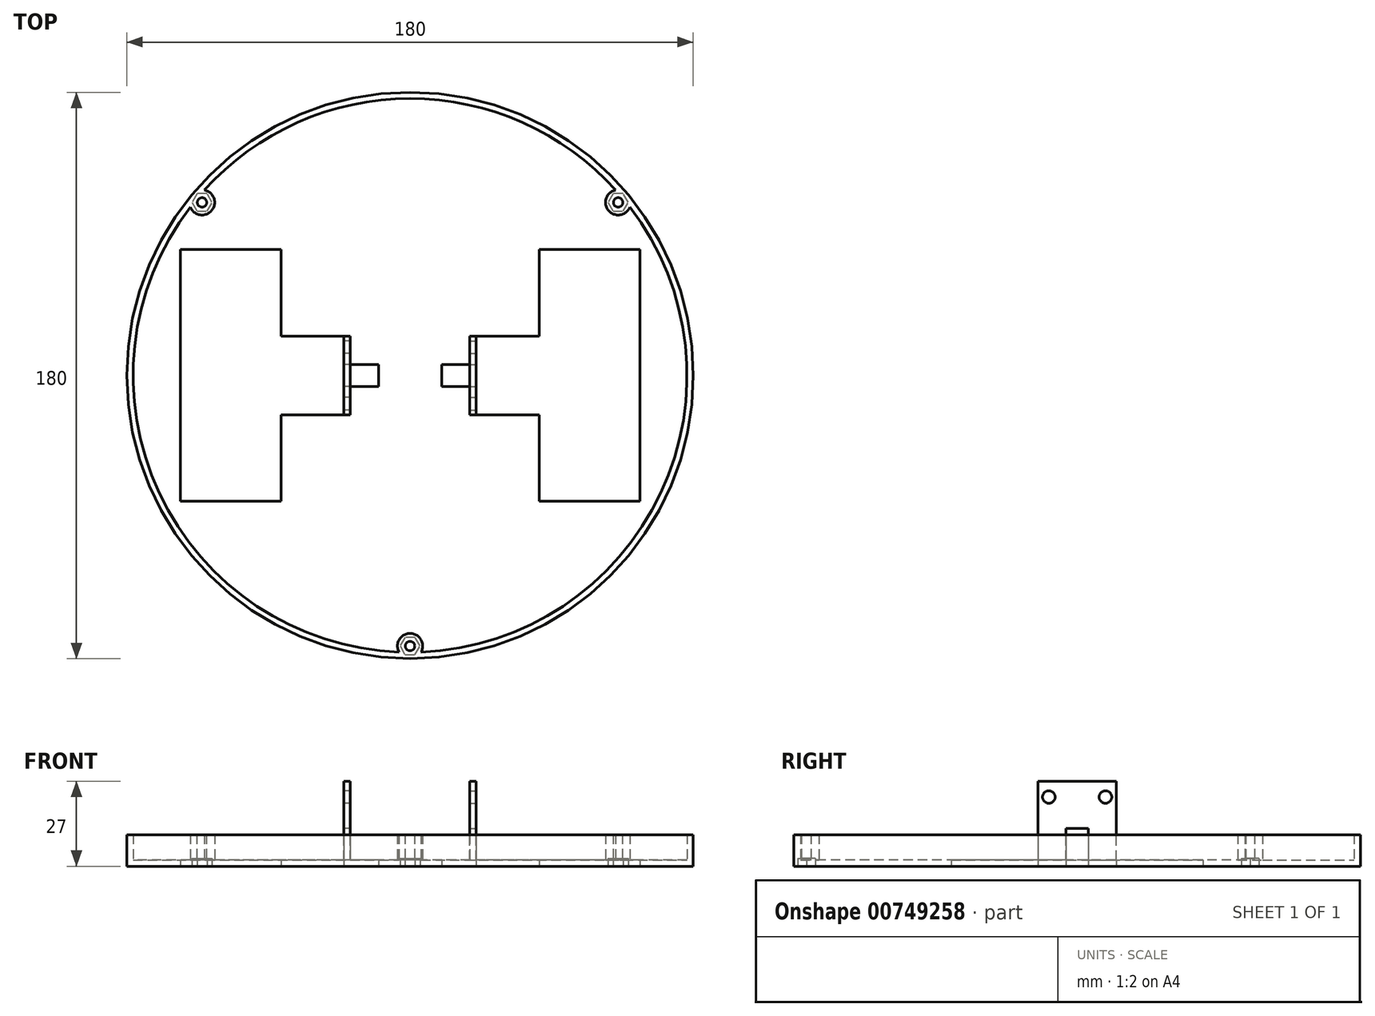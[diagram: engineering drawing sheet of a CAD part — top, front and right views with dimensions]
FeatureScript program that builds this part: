
annotation { "Feature Type Name" : "Feature", "Feature Type Description" : "" }
export const myFeature = defineFeature(function(context is Context, id is Id, definition is map)
    precondition{}
    {
        {
            var Q0;
            Q0=qCreatedBy(makeId("Top.planeOp"),FACE);
            var sketch = newSketch(context, id + "F0", { "sketchPlane" : qUnion([Q0])});
            skCircle(sketch, "E0", {"center": v(0, 0) * mm, "radius": 90 * mm});
            skSolve(sketch);
        }
        {
            var Q0;
            Q0 = qSketchRegion(id + "F0", true);
            var Q1;
            Q1=sQuery(id+"F0.wireOp",EDGE,"E0");
            extrude(context, id + "F1", {"entities" : qUnion([Q0]), "surfaceEntities" : qUnion([Q1]), "depth" : 2 * mm, "offsetDistance" : 25 * mm});
        }
        {
            var Q0;
            Q0=makeQuery(id+"F1.opExtrude","CAP_FACE",FACE,{"disambiguationData":[OSD([sQuery(id+"F0.wireOp",EDGE,"E0")])],"isStart":true});
            var sketch = newSketch(context, id + "F2", { "sketchPlane" : qUnion([Q0])});
            skLineSegment(sketch, "E1", {"start": v(-73, -40) * mm, "end": v(-73, 40) * mm});
            skLineSegment(sketch, "E2", {"start": v(-73, 40) * mm, "end": v(-41, 40) * mm});
            skLineSegment(sketch, "E3", {"start": v(-41, 40) * mm, "end": v(-41, 12.5) * mm});
            skLineSegment(sketch, "E4", {"start": v(-41, 12.5) * mm, "end": v(-21, 12.5) * mm});
            skLineSegment(sketch, "E5", {"start": v(-21, 12.5) * mm, "end": v(-21, 3.5) * mm});
            skLineSegment(sketch, "E6", {"start": v(-21, 3.5) * mm, "end": v(-10, 3.5) * mm});
            skLineSegment(sketch, "E7", {"start": v(-10, 3.5) * mm, "end": v(-10, -3.5) * mm});
            skLineSegment(sketch, "E8", {"start": v(-10, -3.5) * mm, "end": v(-21, -3.5) * mm});
            skLineSegment(sketch, "E9", {"start": v(-21, -3.5) * mm, "end": v(-21, -12.5) * mm});
            skLineSegment(sketch, "E10", {"start": v(-21, -12.5) * mm, "end": v(-41, -12.5) * mm});
            skLineSegment(sketch, "E11", {"start": v(-41, -12.5) * mm, "end": v(-41, -40) * mm});
            skLineSegment(sketch, "E12", {"start": v(-41, -40) * mm, "end": v(-73, -40) * mm});
            skLineSegment(sketch, "E13.MirrorCS", {"start": v(21, -3.5) * mm, "end": v(21, -12.5) * mm});
            skLineSegment(sketch, "E14.MirrorCS", {"start": v(10, 3.5) * mm, "end": v(10, -3.5) * mm});
            skLineSegment(sketch, "E15.MirrorCS", {"start": v(21, 12.5) * mm, "end": v(21, 3.5) * mm});
            skLineSegment(sketch, "E16.MirrorCS", {"start": v(21, 3.5) * mm, "end": v(10, 3.5) * mm});
            skLineSegment(sketch, "E17.MirrorCS", {"start": v(41, -40) * mm, "end": v(73, -40) * mm});
            skLineSegment(sketch, "E18.MirrorCS", {"start": v(41, 40) * mm, "end": v(41, 12.5) * mm});
            skLineSegment(sketch, "E19.MirrorCS", {"start": v(10, -3.5) * mm, "end": v(21, -3.5) * mm});
            skLineSegment(sketch, "E20.MirrorCS", {"start": v(41, 12.5) * mm, "end": v(21, 12.5) * mm});
            skLineSegment(sketch, "E21.MirrorCS", {"start": v(73, -40) * mm, "end": v(73, 40) * mm});
            skLineSegment(sketch, "E22.MirrorCS", {"start": v(21, -12.5) * mm, "end": v(41, -12.5) * mm});
            skLineSegment(sketch, "E23.MirrorCS", {"start": v(73, 40) * mm, "end": v(41, 40) * mm});
            skLineSegment(sketch, "E24.MirrorCS", {"start": v(41, -12.5) * mm, "end": v(41, -40) * mm});
            skSolve(sketch);
        }
        {
            var Q0;
            Q0 = qSketchRegion(id + "F2", true);
            extrude(context, id + "F3", {"entities" : qUnion([Q0]), "operationType" : NewBodyOperationType.REMOVE, "endBound" : BoundingType.THROUGH_ALL, "oppositeDirection" : true, "depth" : 25 * mm, "offsetDistance" : 25 * mm});
        }
        {
            var Q0;
            Q0=makeQuery(id+"F3.boolean.opBoolean","COPY",FACE,{"derivedFrom":makeQuery(id+"F3.opExtrude","SWEPT_FACE",FACE,{"disambiguationData":[OSD([sQuery(id+"F2.wireOp",EDGE,"E5")])]})});
            var sketch = newSketch(context, id + "F4", { "sketchPlane" : qUnion([Q0])});
            skLineSegment(sketch, "E25", {"start": v(-12.5, 2) * mm, "end": v(-12.5, 27) * mm});
            skLineSegment(sketch, "E26", {"start": v(-12.5, 27) * mm, "end": v(12.5, 27) * mm});
            skLineSegment(sketch, "E27", {"start": v(3.5, 2) * mm, "end": v(3.5, 12) * mm});
            skLineSegment(sketch, "E28", {"start": v(3.5, 12) * mm, "end": v(-3.5, 12) * mm});
            skLineSegment(sketch, "E29", {"start": v(-3.5, 12) * mm, "end": v(-3.5, 2) * mm});
            skLineSegment(sketch, "E30", {"start": v(-3.5, 2) * mm, "end": v(-12.5, 2) * mm});
            skPoint(sketch, "E31", {"position": v(12.5, 2) * mm});
            skPoint(sketch, "E32", {"position": v(3.5, 2) * mm});
            skPoint(sketch, "E33", {"position": v(-3.5, 2) * mm});
            skLineSegment(sketch, "E34", {"start": v(12.5, 27) * mm, "end": v(12.5, 2) * mm});
            skLineSegment(sketch, "E35", {"start": v(12.5, 2) * mm, "end": v(3.5, 2) * mm});
            skCircle(sketch, "E36", {"center": v(9, 22) * mm, "radius": 2 * mm});
            skCircle(sketch, "E37", {"center": v(-9, 22) * mm, "radius": 2 * mm});
            skSolve(sketch);
        }
        {
            var Q0;
            Q0 = qSketchRegion(id + "F4", true);
            extrude(context, id + "F5", {"entities" : qUnion([Q0]), "operationType" : NewBodyOperationType.ADD, "oppositeDirection" : true, "depth" : 2 * mm, "offsetDistance" : 25 * mm});
        }
        {
            var Q0;
            Q0=makeQuery(id+"F1.opExtrude","SWEPT_BODY",BODY,{"disambiguationData":[OSD([sQuery(id+"F0.wireOp",EDGE,"E0")])]});
            var Q1;
            Q1=qCreatedBy(makeId("Right.planeOp"),FACE);
            mirror(context, id + "F6", {"operationType" : NewBodyOperationType.ADD, "entities" : qUnion([Q0]), "mirrorPlane" : qUnion([Q1])});
        }
        {
            var Q0;
            Q0=makeQuery(id+"F1.opExtrude","CAP_FACE",FACE,{"disambiguationData":[OSD([sQuery(id+"F0.wireOp",EDGE,"E0")])],"isStart":false});
            var sketch = newSketch(context, id + "F7", { "sketchPlane" : qUnion([Q0])});
            skCircle(sketch, "E38", {"center": v(0, 0) * mm, "radius": 90 * mm});
            skCircle(sketch, "E39", {"center": v(0, 0) * mm, "radius": 88 * mm});
            skSolve(sketch);
        }
        {
            var Q0;
            Q0=makeQuery(id+"F7.imprint","IMPRINT",FACE,{"disambiguationData":[TD([[makeQuery(id+"F7.imprint","IMPRINT",EDGE,{"derivedFrom":sQuery(id+"F7.wireOp",EDGE,"E38")}),1.0]])]});
            extrude(context, id + "F8", {"entities" : qUnion([Q0]), "operationType" : NewBodyOperationType.ADD, "depth" : 8 * mm, "offsetDistance" : 25 * mm});
        }
        {
            var Q0;
            Q0=makeQuery(id+"F1.opExtrude","CAP_FACE",FACE,{"disambiguationData":[OSD([sQuery(id+"F0.wireOp",EDGE,"E0")])],"isStart":false});
            var sketch = newSketch(context, id + "F9", { "sketchPlane" : qUnion([Q0])});
            skCircle(sketch, "E40", {"center": v(66.11, 55) * mm, "radius": 4 * mm});
            skCircle(sketch, "E41", {"center": v(0, -86) * mm, "radius": 4 * mm});
            skCircle(sketch, "E42", {"center": v(-66.11, 55) * mm, "radius": 4 * mm});
            skSolve(sketch);
        }
        {
            var Q0;
            Q0 = qSketchRegion(id + "F9", true);
            extrude(context, id + "F10", {"entities" : qUnion([Q0]), "operationType" : NewBodyOperationType.ADD, "depth" : 8 * mm, "offsetDistance" : 25 * mm});
        }
        {
            var Q0;
            Q0=makeQuery(id+"F10.boolean.opBoolean","MERGE",FACE,{"derivedFrom":[makeQuery(id+"F8.opExtrude","CAP_FACE",FACE,{"disambiguationData":[OSD([sQuery(id+"F7.wireOp",EDGE,"E38"),sQuery(id+"F7.wireOp",EDGE,"E39")])],"isStart":false}),makeQuery(id+"F10.opExtrude","CAP_FACE",FACE,{"disambiguationData":[OSD([sQuery(id+"F9.wireOp",EDGE,"E40")])],"isStart":false}),makeQuery(id+"F10.opExtrude","CAP_FACE",FACE,{"disambiguationData":[OSD([sQuery(id+"F9.wireOp",EDGE,"E41")])],"isStart":false}),makeQuery(id+"F10.opExtrude","CAP_FACE",FACE,{"disambiguationData":[OSD([sQuery(id+"F9.wireOp",EDGE,"R24bcRZv-dxki-Eic6-DGlR-noCj2nAShzK2")])],"isStart":false})]});
            var sketch = newSketch(context, id + "F11", { "sketchPlane" : qUnion([Q0])});
            skCircle(sketch, "E43", {"center": v(-66.11, 55) * mm, "radius": 1.5 * mm});
            skCircle(sketch, "E44", {"center": v(0, -86) * mm, "radius": 1.5 * mm});
            skCircle(sketch, "E45", {"center": v(66.11, 55) * mm, "radius": 1.5 * mm});
            skSolve(sketch);
        }
        {
            var Q0;
            Q0 = qSketchRegion(id + "F11", true);
            extrude(context, id + "F12", {"entities" : qUnion([Q0]), "operationType" : NewBodyOperationType.REMOVE, "endBound" : BoundingType.THROUGH_ALL, "oppositeDirection" : true, "depth" : 25 * mm, "offsetDistance" : 25 * mm});
        }
        {
            var Q0;
            Q0=makeQuery(id+"F1.opExtrude","CAP_FACE",FACE,{"disambiguationData":[OSD([sQuery(id+"F0.wireOp",EDGE,"E0")])],"isStart":true});
            var sketch = newSketch(context, id + "F13", { "sketchPlane" : qUnion([Q0])});
            skCircle(sketch, "E46.0", {"center": v(-66.11, -55) * mm, "radius": 1.5 * mm, "construction": true});
            skCircle(sketch, "E47.cCircle", {"center": v(-66.11, -55) * mm, "radius": 3.2 * mm, "construction": true});
            skLineSegment(sketch, "E47.0", {"start": v(-64.51, -52.23) * mm, "end": v(-62.91, -55) * mm});
            skLineSegment(sketch, "E47.1", {"start": v(-62.91, -55) * mm, "end": v(-64.51, -57.77) * mm});
            skLineSegment(sketch, "E47.2", {"start": v(-64.51, -57.77) * mm, "end": v(-67.71, -57.77) * mm});
            skLineSegment(sketch, "E47.3", {"start": v(-67.71, -57.77) * mm, "end": v(-69.31, -55) * mm});
            skLineSegment(sketch, "E47.4", {"start": v(-69.31, -55) * mm, "end": v(-67.71, -52.23) * mm});
            skLineSegment(sketch, "E47.5", {"start": v(-67.71, -52.23) * mm, "end": v(-64.51, -52.23) * mm});
            skCircle(sketch, "E48.0", {"center": v(66.11, -55) * mm, "radius": 1.5 * mm, "construction": true});
            skCircle(sketch, "E49.cCircle", {"center": v(66.11, -55) * mm, "radius": 3.2 * mm, "construction": true});
            skLineSegment(sketch, "E49.0", {"start": v(67.71, -52.23) * mm, "end": v(69.31, -55) * mm});
            skLineSegment(sketch, "E49.1", {"start": v(69.31, -55) * mm, "end": v(67.71, -57.77) * mm});
            skLineSegment(sketch, "E49.2", {"start": v(67.71, -57.77) * mm, "end": v(64.51, -57.77) * mm});
            skLineSegment(sketch, "E49.3", {"start": v(64.51, -57.77) * mm, "end": v(62.91, -55) * mm});
            skLineSegment(sketch, "E49.4", {"start": v(62.91, -55) * mm, "end": v(64.51, -52.23) * mm});
            skLineSegment(sketch, "E49.5", {"start": v(64.51, -52.23) * mm, "end": v(67.71, -52.23) * mm});
            skCircle(sketch, "E50.0", {"center": v(0, 86) * mm, "radius": 1.5 * mm, "construction": true});
            skCircle(sketch, "E51.cCircle", {"center": v(0, 86) * mm, "radius": 3.2 * mm, "construction": true});
            skLineSegment(sketch, "E51.0", {"start": v(1.6, 88.77) * mm, "end": v(3.2, 86) * mm});
            skLineSegment(sketch, "E51.1", {"start": v(3.2, 86) * mm, "end": v(1.6, 83.23) * mm});
            skLineSegment(sketch, "E51.2", {"start": v(1.6, 83.23) * mm, "end": v(-1.6, 83.23) * mm});
            skLineSegment(sketch, "E51.3", {"start": v(-1.6, 83.23) * mm, "end": v(-3.2, 86) * mm});
            skLineSegment(sketch, "E51.4", {"start": v(-3.2, 86) * mm, "end": v(-1.6, 88.77) * mm});
            skLineSegment(sketch, "E51.5", {"start": v(-1.6, 88.77) * mm, "end": v(1.6, 88.77) * mm});
            skSolve(sketch);
        }
        {
            var Q0;
            Q0 = qSketchRegion(id + "F13", true);
            extrude(context, id + "F14", {"entities" : qUnion([Q0]), "operationType" : NewBodyOperationType.REMOVE, "oppositeDirection" : true, "depth" : 2.5 * mm, "offsetDistance" : 25 * mm});
        }
    });
